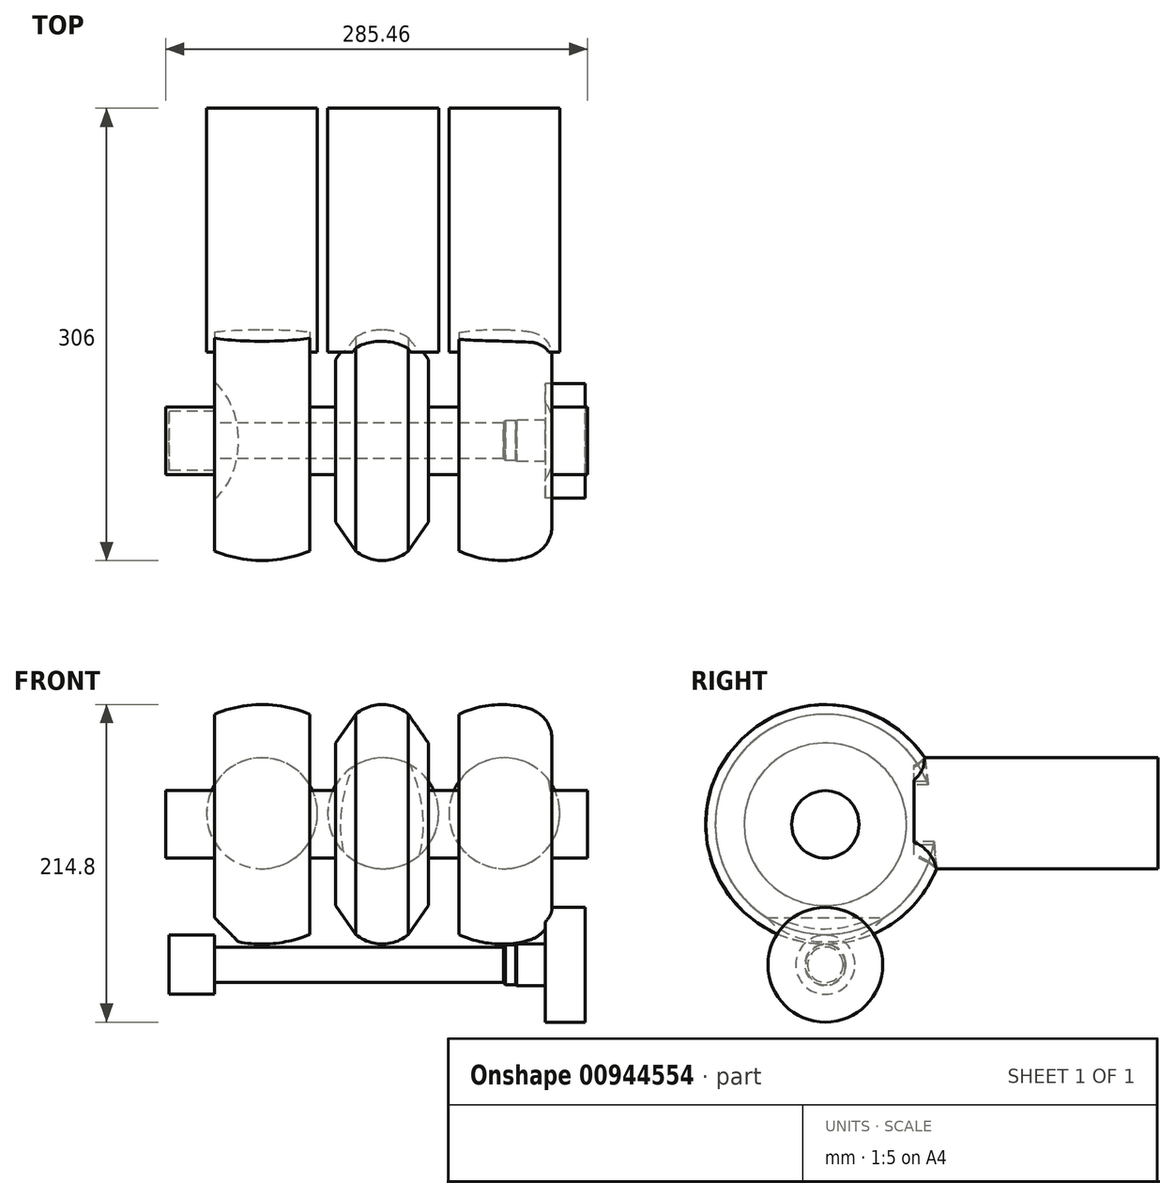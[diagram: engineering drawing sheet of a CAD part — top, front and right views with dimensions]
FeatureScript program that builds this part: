
annotation { "Feature Type Name" : "Feature", "Feature Type Description" : "" }
export const myFeature = defineFeature(function(context is Context, id is Id, definition is map)
    precondition{}
    {
        {
            var Q0;
            Q0=qCreatedBy(makeId("Right.planeOp"),FACE);
            cPlane(context, id + "F0", {"entities" : qUnion([Q0]), "cplaneType" : CPlaneType.OFFSET, "offset" : 82 * mm, "width" : 150 * mm, "height" : 150 * mm});
        }
        {
            var Q0;
            Q0=qCreatedBy(id+"F0.planeOp",FACE);
            cPlane(context, id + "F1", {"entities" : qUnion([Q0]), "cplaneType" : CPlaneType.OFFSET, "offset" : 82 * mm, "width" : 150 * mm, "height" : 150 * mm});
        }
        {
            var Q0;
            Q0=qCreatedBy(makeId("Front.planeOp"),FACE);
            cPlane(context, id + "F2", {"entities" : qUnion([Q0]), "cplaneType" : CPlaneType.OFFSET, "offset" : 60 * mm, "oppositeDirection" : true, "width" : 150 * mm, "height" : 150 * mm});
        }
        {
            var Q0;
            Q0=qCreatedBy(makeId("Right.planeOp"),FACE);
            var sketch = newSketch(context, id + "F3", { "sketchPlane" : qUnion([Q0])});
            skArc(sketch, "E0", {"start": v(-76.5, 0) * mm, "mid": v(0, -76.5) * mm, "end": v(76.5, 0) * mm});
            skArc(sketch, "E1", {"start": v(-22.8, 0) * mm, "mid": v(0, -22.8) * mm, "end": v(22.8, 0) * mm});
            skPoint(sketch, "E2", {"position": v(11.8, -81) * mm});
            skPoint(sketch, "E3", {"position": v(48, -66) * mm});
            skPoint(sketch, "E4", {"position": v(68, -43) * mm});
            skArc(sketch, "E5", {"start": v(110, -26.13) * mm, "mid": v(79.42, -36.3) * mm, "end": v(53.17, -55) * mm, "construction": true});
            skLineSegment(sketch, "E6", {"start": v(110, -26.13) * mm, "end": v(110, 0) * mm});
            skLineSegment(sketch, "E7", {"start": v(110, 0) * mm, "end": v(-76.5, 0) * mm});
            skLineSegment(sketch, "E8", {"start": v(131.9, -37.5) * mm, "end": v(47.02, -37.5) * mm, "construction": true});
            skSolve(sketch);
        }
        {
            var Q0;
            Q0=qCreatedBy(id+"F2.planeOp",FACE);
            var sketch = newSketch(context, id + "F4", { "sketchPlane" : qUnion([Q0])});
            skLineSegment(sketch, "E9", {"start": v(288.38, 7.5) * mm, "end": v(-160.39, 7.5) * mm, "construction": true});
            skCircle(sketch, "E10", {"center": v(0, 7.5) * mm, "radius": 37.5 * mm});
            skCircle(sketch, "E11", {"center": v(82, 7.5) * mm, "radius": 37.5 * mm});
            skCircle(sketch, "E12", {"center": v(164, 7.5) * mm, "radius": 37.5 * mm});
            skSolve(sketch);
        }
        {
            var Q0;
            Q0=qCreatedBy(makeId("Top.planeOp"),FACE);
            var sketch = newSketch(context, id + "F5", { "sketchPlane" : qUnion([Q0])});
            skLineSegment(sketch, "E13", {"start": v(-174.1, 0) * mm, "end": v(247.52, 0) * mm, "construction": true});
            skLineSegment(sketch, "E14", {"start": v(0, -19.96) * mm, "end": v(0, 82.25) * mm, "construction": true});
            skLineSegment(sketch, "E15", {"start": v(82, -22.3) * mm, "end": v(82, 74.78) * mm, "construction": true});
            skLineSegment(sketch, "E16", {"start": v(164, 77.98) * mm, "end": v(164, -26.47) * mm, "construction": true});
            skLineSegment(sketch, "E17.bottom", {"start": v(-65.23, 0) * mm, "end": v(-32.22, 0) * mm});
            skLineSegment(sketch, "E17.top", {"start": v(-65.23, 22.8) * mm, "end": v(-32.22, 22.8) * mm});
            skLineSegment(sketch, "E17.left", {"start": v(-65.23, 0) * mm, "end": v(-65.23, 22.8) * mm});
            skLineSegment(sketch, "E17.right", {"start": v(-32.22, 0) * mm, "end": v(-32.22, 22.8) * mm});
            skLineSegment(sketch, "E18.bottom", {"start": v(32.23, 0) * mm, "end": v(49.83, 0) * mm});
            skLineSegment(sketch, "E18.top", {"start": v(32.23, 22.8) * mm, "end": v(49.83, 22.8) * mm});
            skLineSegment(sketch, "E18.left", {"start": v(32.23, 0) * mm, "end": v(32.23, 22.8) * mm});
            skLineSegment(sketch, "E18.right", {"start": v(49.83, 0) * mm, "end": v(49.83, 22.8) * mm});
            skLineSegment(sketch, "E19.bottom", {"start": v(112.63, 0) * mm, "end": v(133.3, 0) * mm});
            skLineSegment(sketch, "E19.top", {"start": v(112.63, 22.8) * mm, "end": v(133.3, 22.8) * mm});
            skLineSegment(sketch, "E19.left", {"start": v(112.63, 0) * mm, "end": v(112.63, 22.8) * mm});
            skLineSegment(sketch, "E19.right", {"start": v(133.3, 0) * mm, "end": v(133.3, 22.8) * mm});
            skLineSegment(sketch, "E20.bottom", {"start": v(196.23, 0) * mm, "end": v(220.22, 0) * mm});
            skLineSegment(sketch, "E20.top", {"start": v(196.23, 22.8) * mm, "end": v(220.22, 22.8) * mm});
            skLineSegment(sketch, "E20.left", {"start": v(196.23, 0) * mm, "end": v(196.23, 22.8) * mm});
            skLineSegment(sketch, "E20.right", {"start": v(220.22, 0) * mm, "end": v(220.22, 22.8) * mm});
            skLineSegment(sketch, "E21", {"start": v(-32.22, 22.8) * mm, "end": v(-32.23, 74.5) * mm});
            skLineSegment(sketch, "E22", {"start": v(32.23, 22.8) * mm, "end": v(32.23, 74.5) * mm});
            skArc(sketch, "E23", {"start": v(32.23, 74.5) * mm, "mid": v(0, 81) * mm, "end": v(-32.23, 74.5) * mm});
            skLineSegment(sketch, "E24", {"start": v(-32.22, 0) * mm, "end": v(32.23, 0) * mm});
            skLineSegment(sketch, "E25", {"start": v(49.83, 0) * mm, "end": v(112.63, 0) * mm});
            skLineSegment(sketch, "E26", {"start": v(133.3, 0) * mm, "end": v(196.23, 0) * mm});
            skLineSegment(sketch, "E27", {"start": v(49.83, 22.8) * mm, "end": v(49.83, 55) * mm});
            skLineSegment(sketch, "E28", {"start": v(112.63, 22.8) * mm, "end": v(112.63, 55) * mm});
            skLineSegment(sketch, "E29", {"start": v(133.3, 22.8) * mm, "end": v(133.3, 74.5) * mm});
            skLineSegment(sketch, "E30", {"start": v(49.83, 55) * mm, "end": v(63.48, 74.5) * mm});
            skLineSegment(sketch, "E31", {"start": v(112.63, 55) * mm, "end": v(98.98, 74.5) * mm});
            skArc(sketch, "E32", {"start": v(98.98, 74.5) * mm, "mid": v(81.23, 81) * mm, "end": v(63.48, 74.5) * mm});
            skLineSegment(sketch, "E33", {"start": v(-133.57, 81) * mm, "end": v(258.95, 81) * mm, "construction": true});
            skLineSegment(sketch, "E34", {"start": v(196.23, 22.8) * mm, "end": v(196.23, 57.5) * mm});
            skArc(sketch, "E35", {"start": v(196.23, 57.5) * mm, "mid": v(191.8, 70.68) * mm, "end": v(180.3, 78.5) * mm});
            skArc(sketch, "E36", {"start": v(180.3, 78.5) * mm, "mid": v(156.44, 80.76) * mm, "end": v(133.3, 74.5) * mm});
            skSolve(sketch);
        }
        {
            var Q0;
            Q0=makeQuery(id+"F5.imprint","IMPRINT",FACE,{"disambiguationData":[TD([[makeQuery(id+"F5.imprint","IMPRINT",EDGE,{"derivedFrom":sQuery(id+"F5.wireOp",EDGE,"E17.bottom")}),1.0]])]});
            var Q1;
            Q1=makeQuery(id+"F5.imprint","IMPRINT",FACE,{"disambiguationData":[TD([[makeQuery(id+"F5.imprint","IMPRINT",EDGE,{"derivedFrom":sQuery(id+"F5.wireOp",EDGE,"E17.right")}),-1.0]])]});
            var Q2;
            Q2=makeQuery(id+"F5.imprint","IMPRINT",FACE,{"disambiguationData":[TD([[makeQuery(id+"F5.imprint","IMPRINT",EDGE,{"derivedFrom":sQuery(id+"F5.wireOp",EDGE,"E18.bottom")}),1.0]])]});
            var Q3;
            Q3=makeQuery(id+"F5.imprint","IMPRINT",FACE,{"disambiguationData":[TD([[makeQuery(id+"F5.imprint","IMPRINT",EDGE,{"derivedFrom":sQuery(id+"F5.wireOp",EDGE,"E18.right")}),-1.0]])]});
            var Q4;
            Q4=makeQuery(id+"F5.imprint","IMPRINT",FACE,{"disambiguationData":[TD([[makeQuery(id+"F5.imprint","IMPRINT",EDGE,{"derivedFrom":sQuery(id+"F5.wireOp",EDGE,"E19.bottom")}),1.0]])]});
            var Q5;
            Q5=makeQuery(id+"F5.imprint","IMPRINT",FACE,{"disambiguationData":[TD([[makeQuery(id+"F5.imprint","IMPRINT",EDGE,{"derivedFrom":sQuery(id+"F5.wireOp",EDGE,"E19.right")}),-1.0]])]});
            var Q6;
            Q6=makeQuery(id+"F5.imprint","IMPRINT",FACE,{"disambiguationData":[TD([[makeQuery(id+"F5.imprint","IMPRINT",EDGE,{"derivedFrom":sQuery(id+"F5.wireOp",EDGE,"E20.bottom")}),1.0]])]});
            var Q7;
            Q7=sQuery(id+"F5.wireOp",EDGE,"E13");
            revolve(context, id + "F6", {"surfaceOperationType" : NewSurfaceOperationType.NEW, "entities" : qUnion([Q0, Q1, Q2, Q3, Q4, Q5, Q6]), "axis" : qUnion([Q7]), "revolveType" : RevolveType.FULL});
        }
        {
            var Q0;
            Q0=qCreatedBy(id+"F1.planeOp",FACE);
            var sketch = newSketch(context, id + "F7", { "sketchPlane" : qUnion([Q0])});
            skCircle(sketch, "E37", {"center": v(0, 0) * mm, "radius": 76.5 * mm});
            skLineSegment(sketch, "E38", {"start": v(-76.5, 0) * mm, "end": v(76.5, 0) * mm});
            skSolve(sketch);
        }
        {
            var Q0;
            Q0=qCreatedBy(id+"F0.planeOp",FACE);
            var sketch = newSketch(context, id + "F8", { "sketchPlane" : qUnion([Q0])});
            skCircle(sketch, "E39", {"center": v(0, 0) * mm, "radius": 76.5 * mm});
            skLineSegment(sketch, "E40", {"start": v(-76.5, 0) * mm, "end": v(76.5, 0) * mm});
            skSolve(sketch);
        }
        {
            var Q0;
            Q0=makeQuery(id+"F4.imprint","IMPRINT",FACE,{"disambiguationData":[TD([[makeQuery(id+"F4.imprint","IMPRINT",EDGE,{"derivedFrom":sQuery(id+"F4.wireOp",EDGE,"E12")}),1.0]])]});
            var Q1;
            Q1=makeQuery(id+"F4.imprint","IMPRINT",FACE,{"disambiguationData":[TD([[makeQuery(id+"F4.imprint","IMPRINT",EDGE,{"derivedFrom":sQuery(id+"F4.wireOp",EDGE,"E11")}),1.0]])]});
            var Q2;
            Q2=makeQuery(id+"F4.imprint","IMPRINT",FACE,{"disambiguationData":[TD([[makeQuery(id+"F4.imprint","IMPRINT",EDGE,{"derivedFrom":sQuery(id+"F4.wireOp",EDGE,"E10")}),1.0]])]});
            extrude(context, id + "F9", {"entities" : qUnion([Q0, Q1, Q2]), "operationType" : NewBodyOperationType.ADD, "oppositeDirection" : true, "depth" : 165 * mm, "offsetDistance" : 25 * mm});
        }
        {
            var Q0;
            Q0=qCreatedBy(makeId("Top.planeOp"),FACE);
            cPlane(context, id + "F10", {"entities" : qUnion([Q0]), "cplaneType" : CPlaneType.OFFSET, "offset" : 95 * mm, "oppositeDirection" : true, "width" : 150 * mm, "height" : 150 * mm});
        }
        {
            var Q0;
            Q0=qCreatedBy(makeId("Front.planeOp"),FACE);
            var sketch = newSketch(context, id + "F11", { "sketchPlane" : qUnion([Q0])});
            skLineSegment(sketch, "E41", {"start": v(-38, -57.37) * mm, "end": v(-15.37, -80) * mm});
            skLineSegment(sketch, "E42", {"start": v(-15.37, -80) * mm, "end": v(-38, -80) * mm});
            skLineSegment(sketch, "E43", {"start": v(-38, -80) * mm, "end": v(-38, -57.37) * mm});
            skSolve(sketch);
        }
        {
            var Q0;
            Q0=makeQuery(id+"F11.imprint","IMPRINT",FACE,{"disambiguationData":[TD([[makeQuery(id+"F11.imprint","IMPRINT",EDGE,{"derivedFrom":sQuery(id+"F11.wireOp",EDGE,"E41")}),-1.0]])]});
            extrude(context, id + "F12", {"entities" : qUnion([Q0]), "operationType" : NewBodyOperationType.REMOVE, "endBound" : BoundingType.SYMMETRIC, "depth" : 200 * mm, "offsetDistance" : 25 * mm});
        }
        {
            var Q0;
            Q0=qCreatedBy(id+"F10.planeOp",FACE);
            var sketch = newSketch(context, id + "F13", { "sketchPlane" : qUnion([Q0])});
            skLineSegment(sketch, "E44", {"start": v(-80.9, 0) * mm, "end": v(300.52, 0) * mm, "construction": true});
            skLineSegment(sketch, "E45.bottom", {"start": v(-63, 0) * mm, "end": v(-32, 0) * mm});
            skLineSegment(sketch, "E45.top", {"start": v(-63, 20) * mm, "end": v(-32, 20) * mm});
            skLineSegment(sketch, "E45.left", {"start": v(-63, 0) * mm, "end": v(-63, 20) * mm});
            skLineSegment(sketch, "E45.right", {"start": v(-32, 0) * mm, "end": v(-32, 20) * mm});
            skLineSegment(sketch, "E46.bottom", {"start": v(-32, 12) * mm, "end": v(164.8, 12) * mm});
            skLineSegment(sketch, "E46.top", {"start": v(-32, 0) * mm, "end": v(164.8, 0) * mm});
            skLineSegment(sketch, "E46.left", {"start": v(-32, 12) * mm, "end": v(-32, 0) * mm});
            skLineSegment(sketch, "E46.right", {"start": v(164.8, 12) * mm, "end": v(164.8, 0) * mm});
            skLineSegment(sketch, "E47.bottom", {"start": v(164.8, 0) * mm, "end": v(191.8, 0) * mm});
            skLineSegment(sketch, "E47.left", {"start": v(164.8, 0) * mm, "end": v(164.8, 13.5) * mm});
            skLineSegment(sketch, "E47.right", {"start": v(191.8, 0) * mm, "end": v(191.8, 14) * mm});
            skLineSegment(sketch, "E48.bottom", {"start": v(191.8, 0) * mm, "end": v(218.8, 0) * mm});
            skLineSegment(sketch, "E48.top", {"start": v(191.8, 38.8) * mm, "end": v(218.8, 38.8) * mm});
            skLineSegment(sketch, "E48.left", {"start": v(191.8, 0) * mm, "end": v(191.8, 38.8) * mm});
            skLineSegment(sketch, "E48.right", {"start": v(218.8, 0) * mm, "end": v(218.8, 38.8) * mm});
            skLineSegment(sketch, "E49", {"start": v(164.8, 13.5) * mm, "end": v(172.3, 13.5) * mm});
            skLineSegment(sketch, "E50", {"start": v(172.3, 13.5) * mm, "end": v(172.3, 0) * mm});
            skLineSegment(sketch, "E51", {"start": v(172.3, 13.5) * mm, "end": v(172.3, 14) * mm});
            skLineSegment(sketch, "E52", {"start": v(172.3, 14) * mm, "end": v(191.8, 14) * mm});
            skSolve(sketch);
        }
        {
            var Q0;
            {var subQ3=sQuery(id+"F13.wireOp",EDGE,"E48.bottom");Q0=makeQuery(id+"F13.imprint","IMPRINT",FACE,{"disambiguationData":[TD([[makeQuery(id+"F13.imprint","IMPRINT",EDGE,{"derivedFrom":subQ3}),1.0]])]});}
            var Q1;
            {var subQ0=sQuery(id+"F13.wireOp",EDGE,"E50");Q1=makeQuery(id+"F13.imprint","IMPRINT",FACE,{"disambiguationData":[TD([[makeQuery(id+"F13.imprint","IMPRINT",EDGE,{"derivedFrom":subQ0}),1.0]])]});}
            var Q2;
            {var subQ0=sQuery(id+"F13.wireOp",EDGE,"E49");Q2=makeQuery(id+"F13.imprint","IMPRINT",FACE,{"disambiguationData":[TD([[makeQuery(id+"F13.imprint","IMPRINT",EDGE,{"derivedFrom":subQ0}),-1.0]])]});}
            var Q3;
            {var subQ0=sQuery(id+"F13.wireOp",EDGE,"E46.bottom");Q3=makeQuery(id+"F13.imprint","IMPRINT",FACE,{"disambiguationData":[TD([[makeQuery(id+"F13.imprint","IMPRINT",EDGE,{"derivedFrom":subQ0}),-1.0]])]});}
            var Q4;
            Q4=makeQuery(id+"F13.imprint","IMPRINT",FACE,{"disambiguationData":[TD([[makeQuery(id+"F13.imprint","IMPRINT",EDGE,{"derivedFrom":sQuery(id+"F13.wireOp",EDGE,"E45.bottom")}),1.0]])]});
            var Q5;
            Q5=sQuery(id+"F13.wireOp",EDGE,"E44");
            revolve(context, id + "F14", {"operationType" : NewBodyOperationType.ADD, "surfaceOperationType" : NewSurfaceOperationType.NEW, "entities" : qUnion([Q0, Q1, Q2, Q3, Q4]), "axis" : qUnion([Q5]), "revolveType" : RevolveType.FULL});
        }
        {
            var Q0;
            Q0=makeQuery(id+"F14.opRevolve","SWEPT_EDGE",EDGE,{"disambiguationData":[OSD([sQuery(id+"F13.wireOp",EDGE,"E49"),sQuery(id+"F13.wireOp",EDGE,"E50"),sQuery(id+"F13.wireOp",EDGE,"E51")])]});
            chamfer(context, id + "F15", {"entities" : qUnion([Q0]), "width" : 0.5 * mm, "tangentPropagation" : true});
        }
        {
            var Q0;
            Q0=makeQuery(id+"F14.opRevolve","SWEPT_EDGE",EDGE,{"disambiguationData":[OSD([sQuery(id+"F13.wireOp",EDGE,"E46.bottom"),sQuery(id+"F13.wireOp",EDGE,"E47.left")])]});
            chamfer(context, id + "F16", {"entities" : qUnion([Q0]), "width" : 1.5 * mm, "tangentPropagation" : true});
        }
    });
